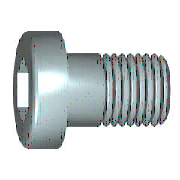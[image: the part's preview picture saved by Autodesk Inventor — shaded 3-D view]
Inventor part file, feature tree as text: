
AUTODESK INVENTOR PART (.ipt)
format: ipt  version: 2020 (Build 240168000, 168)  size: 187,904 bytes
history: native  units: mm (DEFAULTED — no unit token found)
features: sketch x2, chamfer x1, extrude x1, other x1, plane x1
ambient origin geometry x7: Origin, YZ Plane, XY Plane, X Axis, Y Axis, Z Axis, Center Point
bodies: Solid1 (feature_tree), Body (feature_tree)
feature tree (6):
  sketch  "Sketch1"  dims[d0=2.8mm]
  chamfer  "Chamfer2"  Angle=60.0deg  [1 undecoded]
  extrude  "Slot"  Depth=2.0mm
  other  "Work Axis1"
  plane  "Work Plane1"
  sketch  "Sketch2"  dims[d1=1.6mm d2=60.0deg d3=4.0mm d4=3.464102mm d5=7.0mm d10=90.0deg d11=10.0mm d6=0.0mm d7=14.0mm d8=0.0mm d9=0.429415mm d12=0.429415mm d14=0.0mm d15=3.3mm d16=2.0mm d17=25.0mm d28=45.0deg d30=0.0mm d31=0.0mm d32=45.0deg d33=0.4mm d34=90.0deg]
note: 1 required parameter value undecoded (feature->parameter linkage not recoverable at this tier; creation-order binding heuristic only, values carry confidence <= 0.55)
